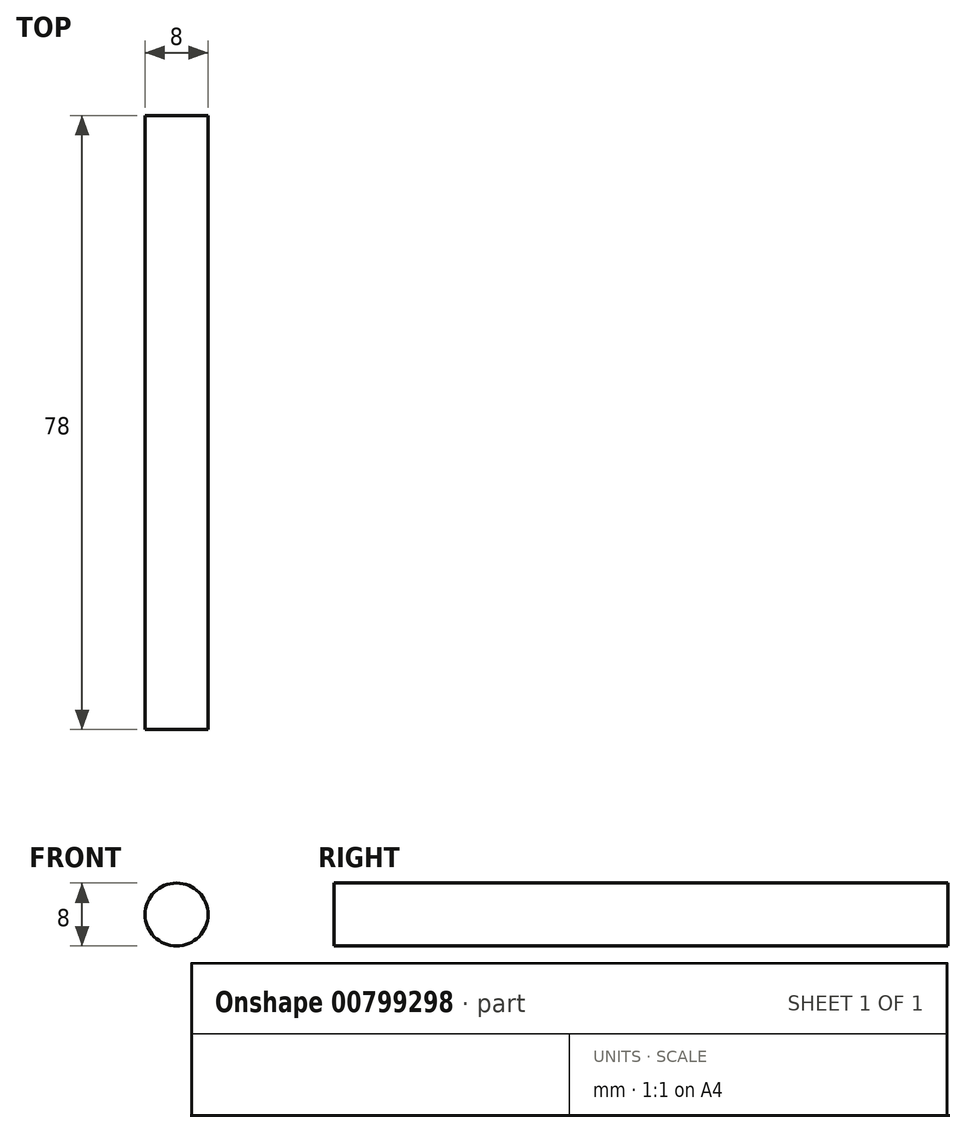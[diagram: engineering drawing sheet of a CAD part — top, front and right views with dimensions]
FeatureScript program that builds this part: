
annotation { "Feature Type Name" : "Feature", "Feature Type Description" : "" }
export const myFeature = defineFeature(function(context is Context, id is Id, definition is map)
    precondition{}
    {
        {
            var Q0;
            Q0=qCreatedBy(makeId("Front.planeOp"),FACE);
            var sketch = newSketch(context, id + "F0", { "sketchPlane" : qUnion([Q0])});
            skCircle(sketch, "E0", {"center": v(0, 0) * mm, "radius": 4 * mm});
            skSolve(sketch);
        }
        {
            var Q0;
            Q0 = qSketchRegion(id + "F0", true);
            extrude(context, id + "F1", {"entities" : qUnion([Q0]), "flatOperationType" : FlatOperationType.REMOVE, "depth" : 78 * mm, "offsetDistance" : 25 * mm, "domain" : OperationDomain.MODEL});
        }
    });
